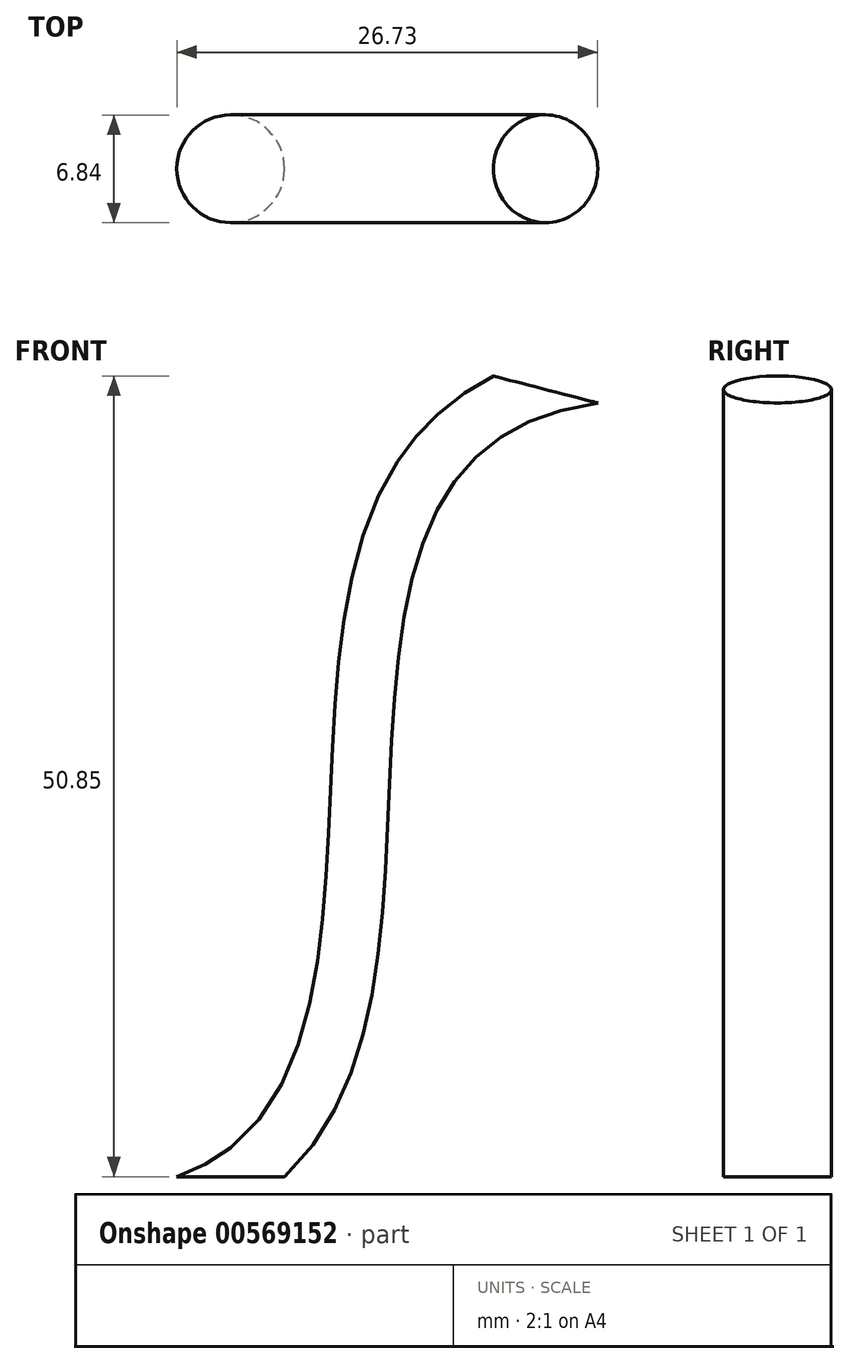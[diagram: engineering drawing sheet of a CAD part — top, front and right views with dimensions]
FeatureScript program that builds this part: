
annotation { "Feature Type Name" : "Feature", "Feature Type Description" : "" }
export const myFeature = defineFeature(function(context is Context, id is Id, definition is map)
    precondition{}
    {
        {
            var Q0;
            Q0=qCreatedBy(makeId("Front.planeOp"),FACE);
            var sketch = newSketch(context, id + "F0", { "sketchPlane" : qUnion([Q0])});
            skFitSpline(sketch, "E0", {"points": [v(0, 0) * mm, v(20, 50) * mm], "startDerivative": vector(46.35, 29.93) * mm, "endDerivative": vector(60, 19.96) * mm});
            skFitSpline(sketch, "E1", {"points": [v(5, 0) * mm, v(20, 48) * mm], "startDerivative": vector(43.82, 36.81) * mm, "endDerivative": vector(-1.04, 33.61) * mm});
            skSolve(sketch);
        }
        {
            var Q0;
            Q0=qCreatedBy(makeId("Top.planeOp"),FACE);
            var sketch = newSketch(context, id + "F1", { "sketchPlane" : qUnion([Q0])});
            skCircle(sketch, "E2", {"center": v(0, 0) * mm, "radius": 3.42 * mm});
            skSolve(sketch);
        }
        {
            var Q0;
            Q0=makeQuery(id+"F1.imprint","IMPRINT",FACE,{"disambiguationData":[TD([[makeQuery(id+"F1.imprint","IMPRINT",EDGE,{"derivedFrom":sQuery(id+"F1.wireOp",EDGE,"E2")}),1.0]])]});
            var Q1;
            Q1=sQuery(id+"F0.wireOp",EDGE,"E0");
            sweep(context, id + "F2", {"profiles" : qUnion([Q0]), "path" : qUnion([Q1])});
        }
    });
